# Revit family: Hager-UNIVERS-Surface_mounted-IP44-With_Cover-With_DIN-NoHosted-PT-pt
name_source: partatom
category: Electrical Equipment
units: mm (PartAtom-declared; Revit-internal decimal feet)

## family parameters
Always vertical = Yes
Cut with Voids When Loaded = No
Maintain Annotation Orientation = No
Panel Configuration = Two Columns, Circuits Across
Part Type = Panelboard
Room Calculation Point = No
Round Connector Dimension = Use Diameter
Shared = No
Work Plane-Based = Yes

## types (43) — shared parameters
Code hager = ADD-EC000214_EU
Default Elevation = 1200 mm
EF000007 - Colour = White
EF000024 - UV resistant = No
EF000049 - Depth = 165 mm
EF000116 - RAL-number = 9010
EF000118 - With mounting plate = No
EF000218 - Built-in depth = 161 mm  [stored 0.528215 ft]
EF001062 - EMC-version = No
EF001088 - Extension possible = Yes
EF001134 - DIN-rail = Yes
EF004462 - Type of closure = Other
EF005474 - Degree of protection (IP) = IP44
EF006306 - With lock = No
EF015941 - Signal passing door = No
ETIM class code = EC000214
ETIM class name = Small distribution board
HG000002-With door or cover = Yes
HG000003-Range = UNIVERS
HG000005-Thickness = 2 mm  [stored 0.00656168 ft]
HG000006-Flush mounted = No
HG000011-Empty rows from bottom = No
HG000012-Door swing angle = 90.00°
HG000013-Door on the left = No
HG000014-Door on the right = Yes
HG000015-Clearance visibility = Yes
HG000016-Door 3D visibility = Yes
HG000017-Distance between poles = 18 mm  [stored 0.0590551 ft]
HG000060-RAL-number = 9010
HG000099-Onfly Template ID = 507532
Manufacturer = Hager
Name BIM&CO = Electricity
Name hager = ADD_Enclosures_EC000214
Reference = Template-Enclosure_EU-EC000214
Uniformat = Low Tension Service & Dist.
Uniformat code = D501001
zero-valued in all types: EF001131 - Inner depth, HG000007-Number of empty columns

## per-type parameters (varying)
| type | BC_METADATA | EF000003 - Mounting method | EF000008 - Width | EF000040 - Height | EF000266 - Number of rows | EF000332 - Built-in height | EF000846 - Built-in width | EF002950 - Width in number of modular spacings | EF006244 - Transparent cover/door | EF009212 - Cover model | EF015776 - Earthing terminal block | EF015777 - Neutral terminal block | HG000001-Number of columns | HG000004-Manufacturer reference | HG000008-Number of empty rows | HG000009-Double swing door | HG000010-Asymmetric doors | HGEF000266-Number of rows | HGEF002950-Width in number of modular spacings |
| UNIVERS-Surface_mounted_W800_H800_D165_36_Modular_Spacing-FWB53N | {"ObjectGuid":"e7c7e345-cd60-4a16-9c19-dfa0064b8dbf","ModelGuid":"5f3c90c3-36aa-4b6e-8de8-4e54ba171ab8","VariantGuid":"0449715e-91fc-4989-86f3-c886387d58d4","Revision":"#3","VariantName":"UNIVERS-Surface_mounted_W800_H800_D165_36_Modular_Spacing-FWB53N"} | Surface mounted | 800 mm  [stored 2.62467 ft] | 800 mm  [stored 2.62467 ft] | 5 | 800 mm  [stored 2.62467 ft] | 800 mm  [stored 2.62467 ft] | 36 | No | With notch | No | No | 3 | FWB53N | 2 | Yes | Yes | 5 | 36 |
| UNIVERS-Surface_mounted_W800_H800_D165_36_Modular_Spacing-FWB53S | {"ObjectGuid":"e7c7e345-cd60-4a16-9c19-dfa0064b8dbf","ModelGuid":"5f3c90c3-36aa-4b6e-8de8-4e54ba171ab8","VariantGuid":"70780475-1a53-44c7-8c09-04e4199d2f75","Revision":"#3","VariantName":"UNIVERS-Surface_mounted_W800_H800_D165_36_Modular_Spacing-FWB53S"} | Surface mounted | 800 mm  [stored 2.62467 ft] | 800 mm  [stored 2.62467 ft] | 5 | 800 mm  [stored 2.62467 ft] | 800 mm  [stored 2.62467 ft] | 36 | No | With notch | Yes | Yes | 3 | FWB53S | 0 | Yes | Yes | 5 | 36 |
| UNIVERS-Surface_mounted_W1050_H800_D165_48_Modular_Spacing-FWB54GS | {"ObjectGuid":"e7c7e345-cd60-4a16-9c19-dfa0064b8dbf","ModelGuid":"5f3c90c3-36aa-4b6e-8de8-4e54ba171ab8","VariantGuid":"5e6222b7-83c6-47e9-85ec-fb5e80a4b5de","Revision":"#3","VariantName":"UNIVERS-Surface_mounted_W1050_H800_D165_48_Modular_Spacing-FWB54GS"} | Surface mounted | 1050 mm  [stored 3.44488 ft] | 800 mm  [stored 2.62467 ft] | 5 | 800 mm  [stored 2.62467 ft] | 1050 mm  [stored 3.44488 ft] | 48 | Yes | With notch | Yes | Yes | 4 | FWB54GS | 0 | Yes | No | 5 | 48 |
| UNIVERS-Surface_mounted_W1050_H800_D165_48_Modular_Spacing-FWB54S | {"ObjectGuid":"e7c7e345-cd60-4a16-9c19-dfa0064b8dbf","ModelGuid":"5f3c90c3-36aa-4b6e-8de8-4e54ba171ab8","VariantGuid":"4e09de71-0c15-486c-be22-81b695f3b53c","Revision":"#3","VariantName":"UNIVERS-Surface_mounted_W1050_H800_D165_48_Modular_Spacing-FWB54S"} | Surface mounted | 1050 mm  [stored 3.44488 ft] | 800 mm  [stored 2.62467 ft] | 5 | 800 mm  [stored 2.62467 ft] | 1050 mm  [stored 3.44488 ft] | 48 | No | With notch | Yes | Yes | 4 | FWB54S | 0 | Yes | No | 5 | 48 |
| UNIVERS-Surface_mounted_W300_H950_D165_12_Modular_Spacing-FWB61S | {"ObjectGuid":"e7c7e345-cd60-4a16-9c19-dfa0064b8dbf","ModelGuid":"5f3c90c3-36aa-4b6e-8de8-4e54ba171ab8","VariantGuid":"d75a9c82-e212-4b1c-91cf-2a02521cf286","Revision":"#3","VariantName":"UNIVERS-Surface_mounted_W300_H950_D165_12_Modular_Spacing-FWB61S"} | Surface mounted | 300 mm | 950 mm  [stored 3.1168 ft] | 6 | 950 mm  [stored 3.1168 ft] | 300 mm | 12 | No | With notch | Yes | Yes | 1 | FWB61S | 0 | No | No | 6 | 12 |
| UNIVERS-Surface_mounted_W550_H950_D165_24_Modular_Spacing-FWB62GS | {"ObjectGuid":"e7c7e345-cd60-4a16-9c19-dfa0064b8dbf","ModelGuid":"5f3c90c3-36aa-4b6e-8de8-4e54ba171ab8","VariantGuid":"d2d455f6-8088-4d0c-b9d0-a91f4a603c26","Revision":"#3","VariantName":"UNIVERS-Surface_mounted_W550_H950_D165_24_Modular_Spacing-FWB62GS"} | Surface mounted | 550 mm | 950 mm  [stored 3.1168 ft] | 6 | 950 mm  [stored 3.1168 ft] | 550 mm | 24 | Yes | With notch | Yes | Yes | 2 | FWB62GS | 0 | No | No | 6 | 24 |
| UNIVERS-Surface_mounted_W550_H950_D165_26_Modular_Spacing-FWB62M2 | {"ObjectGuid":"e7c7e345-cd60-4a16-9c19-dfa0064b8dbf","ModelGuid":"5f3c90c3-36aa-4b6e-8de8-4e54ba171ab8","VariantGuid":"2e5a0d4c-b45d-4552-9a05-bd38f025c8f6","Revision":"#3","VariantName":"UNIVERS-Surface_mounted_W550_H950_D165_26_Modular_Spacing-FWB62M2"} | Surface mounted | 550 mm | 950 mm  [stored 3.1168 ft] | 6 | 950 mm  [stored 3.1168 ft] | 550 mm | 26 | No | Closed | No | No | 1 | FWB62M2 | 0 | No | No | 6 | 26 |
| UNIVERS-Surface_mounted_W550_H950_D165_24_Modular_Spacing-FWB62N | {"ObjectGuid":"e7c7e345-cd60-4a16-9c19-dfa0064b8dbf","ModelGuid":"5f3c90c3-36aa-4b6e-8de8-4e54ba171ab8","VariantGuid":"0534ccd4-eb5c-456c-84bc-d0c8a7f9486a","Revision":"#3","VariantName":"UNIVERS-Surface_mounted_W550_H950_D165_24_Modular_Spacing-FWB62N"} | Surface mounted | 550 mm | 950 mm  [stored 3.1168 ft] | 6 | 950 mm  [stored 3.1168 ft] | 550 mm | 24 | No | With notch | No | No | 2 | FWB62N | 2 | No | No | 6 | 24 |
| UNIVERS-Surface_mounted_W300_H500_D165_12_Modular_Spacing-FWB31S | {"ObjectGuid":"e7c7e345-cd60-4a16-9c19-dfa0064b8dbf","ModelGuid":"5f3c90c3-36aa-4b6e-8de8-4e54ba171ab8","VariantGuid":"9bf5f36f-aab7-4db9-9452-cf65efd598aa","Revision":"#3","VariantName":"UNIVERS-Surface_mounted_W300_H500_D165_12_Modular_Spacing-FWB31S"} | Surface mounted | 300 mm | 500 mm  [stored 1.64042 ft] | 3 | 500 mm  [stored 1.64042 ft] | 300 mm | 12 | No | With notch | Yes | Yes | 1 | FWB31S | 0 | No | No | 3 | 12 |
| UNIVERS-Surface_mounted_W550_H500_D165_24_Modular_Spacing-FWB32GS | {"ObjectGuid":"e7c7e345-cd60-4a16-9c19-dfa0064b8dbf","ModelGuid":"5f3c90c3-36aa-4b6e-8de8-4e54ba171ab8","VariantGuid":"fb7a85dd-3230-4837-b0c0-b72064a3e6fe","Revision":"#3","VariantName":"UNIVERS-Surface_mounted_W550_H500_D165_24_Modular_Spacing-FWB32GS"} | Surface mounted | 550 mm | 500 mm  [stored 1.64042 ft] | 3 | 500 mm  [stored 1.64042 ft] | 550 mm | 24 | Yes | With notch | Yes | Yes | 2 | FWB32GS | 0 | No | No | 3 | 24 |
| UNIVERS-Surface_mounted_W550_H500_D165_26_Modular_Spacing-FWB32M2 | {"ObjectGuid":"e7c7e345-cd60-4a16-9c19-dfa0064b8dbf","ModelGuid":"5f3c90c3-36aa-4b6e-8de8-4e54ba171ab8","VariantGuid":"f52a0b61-ad72-444d-9360-4d9b0c4974fd","Revision":"#3","VariantName":"UNIVERS-Surface_mounted_W550_H500_D165_26_Modular_Spacing-FWB32M2"} | Surface mounted | 550 mm | 500 mm  [stored 1.64042 ft] | 3 | 500 mm  [stored 1.64042 ft] | 550 mm | 26 | No | Closed | No | No | 1 | FWB32M2 | 0 | No | No | 3 | 26 |
| UNIVERS-Surface_mounted_W550_H500_D165_24_Modular_Spacing-FWB32S | {"ObjectGuid":"e7c7e345-cd60-4a16-9c19-dfa0064b8dbf","ModelGuid":"5f3c90c3-36aa-4b6e-8de8-4e54ba171ab8","VariantGuid":"5a80b1ac-59b3-4e31-a08f-5cec29b1deb8","Revision":"#3","VariantName":"UNIVERS-Surface_mounted_W550_H500_D165_24_Modular_Spacing-FWB32S"} | Surface mounted | 550 mm | 500 mm  [stored 1.64042 ft] | 3 | 500 mm  [stored 1.64042 ft] | 550 mm | 24 | No | With notch | Yes | Yes | 2 | FWB32S | 0 | No | No | 3 | 24 |
| UNIVERS-Surface_mounted_W800_H500_D165_36_Modular_Spacing-FWB33S | {"ObjectGuid":"e7c7e345-cd60-4a16-9c19-dfa0064b8dbf","ModelGuid":"5f3c90c3-36aa-4b6e-8de8-4e54ba171ab8","VariantGuid":"35a470b6-89d0-4b4f-96af-1046d63bd483","Revision":"#3","VariantName":"UNIVERS-Surface_mounted_W800_H500_D165_36_Modular_Spacing-FWB33S"} | Surface mounted | 800 mm  [stored 2.62467 ft] | 500 mm  [stored 1.64042 ft] | 3 | 500 mm  [stored 1.64042 ft] | 800 mm  [stored 2.62467 ft] | 36 | No | With notch | Yes | Yes | 3 | FWB33S | 0 | Yes | Yes | 3 | 36 |
| UNIVERS-Surface_mounted_W1050_H500_D165_48_Modular_Spacing-FWB34GS | {"ObjectGuid":"e7c7e345-cd60-4a16-9c19-dfa0064b8dbf","ModelGuid":"5f3c90c3-36aa-4b6e-8de8-4e54ba171ab8","VariantGuid":"be8cd02b-23f5-4942-b7b3-b5a2112c5854","Revision":"#3","VariantName":"UNIVERS-Surface_mounted_W1050_H500_D165_48_Modular_Spacing-FWB34GS"} | Surface mounted | 1050 mm  [stored 3.44488 ft] | 500 mm  [stored 1.64042 ft] | 3 | 500 mm  [stored 1.64042 ft] | 1050 mm  [stored 3.44488 ft] | 48 | Yes | With notch | Yes | Yes | 4 | FWB34GS | 0 | Yes | No | 3 | 48 |
| UNIVERS-Surface_mounted_W1050_H500_D165_48_Modular_Spacing-FWB34S | {"ObjectGuid":"e7c7e345-cd60-4a16-9c19-dfa0064b8dbf","ModelGuid":"5f3c90c3-36aa-4b6e-8de8-4e54ba171ab8","VariantGuid":"cc12be3d-891f-44bf-81d6-319a16d03e2f","Revision":"#3","VariantName":"UNIVERS-Surface_mounted_W1050_H500_D165_48_Modular_Spacing-FWB34S"} | Surface mounted | 1050 mm  [stored 3.44488 ft] | 500 mm  [stored 1.64042 ft] | 3 | 500 mm  [stored 1.64042 ft] | 1050 mm  [stored 3.44488 ft] | 48 | No | With notch | Yes | Yes | 4 | FWB34S | 0 | Yes | No | 3 | 48 |
| UNIVERS-Surface_mounted_W300_H650_D165_12_Modular_Spacing-FWB41S | {"ObjectGuid":"e7c7e345-cd60-4a16-9c19-dfa0064b8dbf","ModelGuid":"5f3c90c3-36aa-4b6e-8de8-4e54ba171ab8","VariantGuid":"5ece5d32-3d52-4811-be08-8941b2c84f9b","Revision":"#3","VariantName":"UNIVERS-Surface_mounted_W300_H650_D165_12_Modular_Spacing-FWB41S"} | Surface mounted | 300 mm | 650 mm  [stored 2.13255 ft] | 4 | 650 mm  [stored 2.13255 ft] | 300 mm | 12 | No | With notch | Yes | Yes | 1 | FWB41S | 0 | No | No | 4 | 12 |
| UNIVERS-Surface_mounted_W550_H650_D165_24_Modular_Spacing-FWB42GS | {"ObjectGuid":"e7c7e345-cd60-4a16-9c19-dfa0064b8dbf","ModelGuid":"5f3c90c3-36aa-4b6e-8de8-4e54ba171ab8","VariantGuid":"4800a197-08de-4eea-944b-05a1431e3091","Revision":"#3","VariantName":"UNIVERS-Surface_mounted_W550_H650_D165_24_Modular_Spacing-FWB42GS"} | Surface mounted | 550 mm | 650 mm  [stored 2.13255 ft] | 4 | 650 mm  [stored 2.13255 ft] | 550 mm | 24 | Yes | With notch | Yes | Yes | 2 | FWB42GS | 0 | No | No | 4 | 24 |
| UNIVERS-Surface_mounted_W550_H650_D165_26_Modular_Spacing-FWB42M2 | {"ObjectGuid":"e7c7e345-cd60-4a16-9c19-dfa0064b8dbf","ModelGuid":"5f3c90c3-36aa-4b6e-8de8-4e54ba171ab8","VariantGuid":"ff45878f-ee16-4e91-9788-272bdf2cb385","Revision":"#3","VariantName":"UNIVERS-Surface_mounted_W550_H650_D165_26_Modular_Spacing-FWB42M2"} | Surface mounted | 550 mm | 650 mm  [stored 2.13255 ft] | 4 | 650 mm  [stored 2.13255 ft] | 550 mm | 26 | No | Closed | No | No | 1 | FWB42M2 | 0 | No | No | 4 | 26 |
| UNIVERS-Surface_mounted_W550_H650_D165_24_Modular_Spacing-FWB42S | {"ObjectGuid":"e7c7e345-cd60-4a16-9c19-dfa0064b8dbf","ModelGuid":"5f3c90c3-36aa-4b6e-8de8-4e54ba171ab8","VariantGuid":"a7ff8edd-fea0-4138-8384-63f245e46ff6","Revision":"#3","VariantName":"UNIVERS-Surface_mounted_W550_H650_D165_24_Modular_Spacing-FWB42S"} | Surface mounted/recessed mounted | 550 mm | 650 mm  [stored 2.13255 ft] | 4 | 650 mm  [stored 2.13255 ft] | 550 mm | 24 | No | With notch | Yes | Yes | 2 | FWB42S | 0 | No | No | 4 | 24 |
| UNIVERS-Surface_mounted_W800_H650_D165_36_Modular_Spacing-FWB43S | {"ObjectGuid":"e7c7e345-cd60-4a16-9c19-dfa0064b8dbf","ModelGuid":"5f3c90c3-36aa-4b6e-8de8-4e54ba171ab8","VariantGuid":"694371a0-3cfb-4381-bc54-f25bbc3fdddb","Revision":"#3","VariantName":"UNIVERS-Surface_mounted_W800_H650_D165_36_Modular_Spacing-FWB43S"} | Surface mounted | 800 mm  [stored 2.62467 ft] | 650 mm  [stored 2.13255 ft] | 4 | 650 mm  [stored 2.13255 ft] | 800 mm  [stored 2.62467 ft] | 36 | No | With notch | Yes | Yes | 3 | FWB43S | 0 | Yes | Yes | 4 | 36 |
| UNIVERS-Surface_mounted_W1050_H650_D165_48_Modular_Spacing-FWB44GS | {"ObjectGuid":"e7c7e345-cd60-4a16-9c19-dfa0064b8dbf","ModelGuid":"5f3c90c3-36aa-4b6e-8de8-4e54ba171ab8","VariantGuid":"80b9d9d5-fd64-4f73-886d-269bf54e62dc","Revision":"#3","VariantName":"UNIVERS-Surface_mounted_W1050_H650_D165_48_Modular_Spacing-FWB44GS"} | Surface mounted | 1050 mm  [stored 3.44488 ft] | 650 mm  [stored 2.13255 ft] | 4 | 650 mm  [stored 2.13255 ft] | 1050 mm  [stored 3.44488 ft] | 48 | Yes | With notch | Yes | Yes | 4 | FWB44GS | 0 | Yes | No | 4 | 48 |
| UNIVERS-Surface_mounted_W1050_H650_D165_48_Modular_Spacing-FWB44S | {"ObjectGuid":"e7c7e345-cd60-4a16-9c19-dfa0064b8dbf","ModelGuid":"5f3c90c3-36aa-4b6e-8de8-4e54ba171ab8","VariantGuid":"958c4d4e-67ea-4ca2-b1af-8047328ca48a","Revision":"#3","VariantName":"UNIVERS-Surface_mounted_W1050_H650_D165_48_Modular_Spacing-FWB44S"} | Surface mounted | 1050 mm  [stored 3.44488 ft] | 650 mm  [stored 2.13255 ft] | 4 | 650 mm  [stored 2.13255 ft] | 1050 mm  [stored 3.44488 ft] | 48 | No | With notch | Yes | Yes | 4 | FWB44S | 0 | Yes | No | 4 | 48 |
| UNIVERS-Surface_mounted_W300_H800_D165_12_Modular_Spacing-FWB51S | {"ObjectGuid":"e7c7e345-cd60-4a16-9c19-dfa0064b8dbf","ModelGuid":"5f3c90c3-36aa-4b6e-8de8-4e54ba171ab8","VariantGuid":"485017d3-d1a1-4c50-9960-5198ff632122","Revision":"#3","VariantName":"UNIVERS-Surface_mounted_W300_H800_D165_12_Modular_Spacing-FWB51S"} | Surface mounted | 300 mm | 800 mm  [stored 2.62467 ft] | 5 | 800 mm  [stored 2.62467 ft] | 300 mm | 12 | No | With notch | Yes | Yes | 1 | FWB51S | 0 | No | No | 5 | 12 |
| UNIVERS-Surface_mounted_W550_H800_D165_24_Modular_Spacing-FWB52GS | {"ObjectGuid":"e7c7e345-cd60-4a16-9c19-dfa0064b8dbf","ModelGuid":"5f3c90c3-36aa-4b6e-8de8-4e54ba171ab8","VariantGuid":"8440c55c-928c-4a66-a384-c63e5e9be550","Revision":"#3","VariantName":"UNIVERS-Surface_mounted_W550_H800_D165_24_Modular_Spacing-FWB52GS"} | Surface mounted | 550 mm | 800 mm  [stored 2.62467 ft] | 5 | 800 mm  [stored 2.62467 ft] | 550 mm | 24 | Yes | With notch | Yes | Yes | 2 | FWB52GS | 0 | No | No | 5 | 24 |
| UNIVERS-Surface_mounted_W550_H800_D165_26_Modular_Spacing-FWB52M2 | {"ObjectGuid":"e7c7e345-cd60-4a16-9c19-dfa0064b8dbf","ModelGuid":"5f3c90c3-36aa-4b6e-8de8-4e54ba171ab8","VariantGuid":"84c6e0b0-84ba-43f9-8486-ac857d178bdd","Revision":"#3","VariantName":"UNIVERS-Surface_mounted_W550_H800_D165_26_Modular_Spacing-FWB52M2"} | Surface mounted | 550 mm | 800 mm  [stored 2.62467 ft] | 5 | 800 mm  [stored 2.62467 ft] | 550 mm | 26 | No | Closed | No | No | 1 | FWB52M2 | 0 | No | No | 5 | 26 |
| UNIVERS-Surface_mounted_W550_H800_D165_24_Modular_Spacing-FWB52N | {"ObjectGuid":"e7c7e345-cd60-4a16-9c19-dfa0064b8dbf","ModelGuid":"5f3c90c3-36aa-4b6e-8de8-4e54ba171ab8","VariantGuid":"eb04def6-35ae-4f01-a42c-74ccab6b1dd4","Revision":"#3","VariantName":"UNIVERS-Surface_mounted_W550_H800_D165_24_Modular_Spacing-FWB52N"} | Surface mounted | 550 mm | 800 mm  [stored 2.62467 ft] | 5 | 800 mm  [stored 2.62467 ft] | 550 mm | 24 | No | With notch | No | No | 2 | FWB52N | 2 | No | No | 5 | 24 |
| UNIVERS-Surface_mounted_W550_H800_D165_24_Modular_Spacing-FWB52S | {"ObjectGuid":"e7c7e345-cd60-4a16-9c19-dfa0064b8dbf","ModelGuid":"5f3c90c3-36aa-4b6e-8de8-4e54ba171ab8","VariantGuid":"11957740-69cf-4a1b-bfa0-25a853491458","Revision":"#3","VariantName":"UNIVERS-Surface_mounted_W550_H800_D165_24_Modular_Spacing-FWB52S"} | Surface mounted | 550 mm | 800 mm  [stored 2.62467 ft] | 5 | 800 mm  [stored 2.62467 ft] | 550 mm | 24 | No | With notch | Yes | Yes | 2 | FWB52S | 0 | No | No | 5 | 24 |
| UNIVERS-Surface_mounted_W550_H950_D165_24_Modular_Spacing-FWB62S | {"ObjectGuid":"e7c7e345-cd60-4a16-9c19-dfa0064b8dbf","ModelGuid":"5f3c90c3-36aa-4b6e-8de8-4e54ba171ab8","VariantGuid":"77259382-65aa-4b1e-869a-cfa50e7e1151","Revision":"#3","VariantName":"UNIVERS-Surface_mounted_W550_H950_D165_24_Modular_Spacing-FWB62S"} | Surface mounted | 550 mm | 950 mm  [stored 3.1168 ft] | 6 | 950 mm  [stored 3.1168 ft] | 550 mm | 24 | No | With notch | Yes | Yes | 2 | FWB62S | 0 | No | No | 6 | 24 |
| UNIVERS-Surface_mounted_W800_H950_D165_36_Modular_Spacing-FWB63N | {"ObjectGuid":"e7c7e345-cd60-4a16-9c19-dfa0064b8dbf","ModelGuid":"5f3c90c3-36aa-4b6e-8de8-4e54ba171ab8","VariantGuid":"cb41e5b3-02c2-4750-a6e5-7048ffe01e97","Revision":"#3","VariantName":"UNIVERS-Surface_mounted_W800_H950_D165_36_Modular_Spacing-FWB63N"} | Surface mounted | 800 mm  [stored 2.62467 ft] | 950 mm  [stored 3.1168 ft] | 6 | 950 mm  [stored 3.1168 ft] | 800 mm  [stored 2.62467 ft] | 36 | No | With notch | No | No | 3 | FWB63N | 2 | Yes | Yes | 6 | 36 |
| UNIVERS-Surface_mounted_W800_H950_D165_36_Modular_Spacing-FWB63S | {"ObjectGuid":"e7c7e345-cd60-4a16-9c19-dfa0064b8dbf","ModelGuid":"5f3c90c3-36aa-4b6e-8de8-4e54ba171ab8","VariantGuid":"f41a47f8-f480-46dd-a0ef-3e98abfe04c0","Revision":"#3","VariantName":"UNIVERS-Surface_mounted_W800_H950_D165_36_Modular_Spacing-FWB63S"} | Surface mounted | 800 mm  [stored 2.62467 ft] | 950 mm  [stored 3.1168 ft] | 6 | 950 mm  [stored 3.1168 ft] | 800 mm  [stored 2.62467 ft] | 36 | No | With notch | Yes | Yes | 3 | FWB63S | 0 | Yes | Yes | 6 | 36 |
| UNIVERS-Surface_mounted_W1050_H950_D165_48_Modular_Spacing-FWB64GS | {"ObjectGuid":"e7c7e345-cd60-4a16-9c19-dfa0064b8dbf","ModelGuid":"5f3c90c3-36aa-4b6e-8de8-4e54ba171ab8","VariantGuid":"3c734a3f-374f-4c5e-822b-aceaff54270b","Revision":"#3","VariantName":"UNIVERS-Surface_mounted_W1050_H950_D165_48_Modular_Spacing-FWB64GS"} | Surface mounted | 1050 mm  [stored 3.44488 ft] | 950 mm  [stored 3.1168 ft] | 6 | 950 mm  [stored 3.1168 ft] | 1050 mm  [stored 3.44488 ft] | 48 | Yes | With notch | Yes | Yes | 4 | FWB64GS | 0 | Yes | No | 6 | 48 |
| UNIVERS-Surface_mounted_W1050_H950_D165_48_Modular_Spacing-FWB64N | {"ObjectGuid":"e7c7e345-cd60-4a16-9c19-dfa0064b8dbf","ModelGuid":"5f3c90c3-36aa-4b6e-8de8-4e54ba171ab8","VariantGuid":"99b5a869-c00c-4308-92dd-7e31dc713ef3","Revision":"#3","VariantName":"UNIVERS-Surface_mounted_W1050_H950_D165_48_Modular_Spacing-FWB64N"} | Surface mounted | 1050 mm  [stored 3.44488 ft] | 950 mm  [stored 3.1168 ft] | 6 | 950 mm  [stored 3.1168 ft] | 1050 mm  [stored 3.44488 ft] | 48 | No | With notch | No | No | 4 | FWB64N | 2 | Yes | No | 6 | 48 |
| UNIVERS-Surface_mounted_W1050_H950_D165_48_Modular_Spacing-FWB64S | {"ObjectGuid":"e7c7e345-cd60-4a16-9c19-dfa0064b8dbf","ModelGuid":"5f3c90c3-36aa-4b6e-8de8-4e54ba171ab8","VariantGuid":"fc1a7d38-a105-4c3a-b171-c45a80d5c211","Revision":"#3","VariantName":"UNIVERS-Surface_mounted_W1050_H950_D165_48_Modular_Spacing-FWB64S"} | Surface mounted | 1050 mm  [stored 3.44488 ft] | 950 mm  [stored 3.1168 ft] | 6 | 950 mm  [stored 3.1168 ft] | 1050 mm  [stored 3.44488 ft] | 48 | No | With notch | Yes | Yes | 4 | FWB64S | 0 | Yes | No | 6 | 48 |
| UNIVERS-Surface_mounted_W300_H1100_D165_12_Modular_Spacing-FWB71S | {"ObjectGuid":"e7c7e345-cd60-4a16-9c19-dfa0064b8dbf","ModelGuid":"5f3c90c3-36aa-4b6e-8de8-4e54ba171ab8","VariantGuid":"1162c4e2-4707-4c66-80c0-3641417c3d5d","Revision":"#3","VariantName":"UNIVERS-Surface_mounted_W300_H1100_D165_12_Modular_Spacing-FWB71S"} | Surface mounted | 300 mm | 1100 mm | 7 | 1100 mm | 300 mm | 12 | No | With notch | Yes | Yes | 1 | FWB71S | 0 | No | No | 7 | 12 |
| UNIVERS-Surface_mounted_W550_H1100_D165_24_Modular_Spacing-FWB72GS | {"ObjectGuid":"e7c7e345-cd60-4a16-9c19-dfa0064b8dbf","ModelGuid":"5f3c90c3-36aa-4b6e-8de8-4e54ba171ab8","VariantGuid":"1073677e-2332-4886-b88c-450902d7afb2","Revision":"#3","VariantName":"UNIVERS-Surface_mounted_W550_H1100_D165_24_Modular_Spacing-FWB72GS"} | Surface mounted | 550 mm | 1100 mm | 7 | 1100 mm | 550 mm | 24 | Yes | With notch | Yes | Yes | 2 | FWB72GS | 0 | No | No | 7 | 24 |
| UNIVERS-Surface_mounted_W550_H1100_D165_26_Modular_Spacing-FWB72M2 | {"ObjectGuid":"e7c7e345-cd60-4a16-9c19-dfa0064b8dbf","ModelGuid":"5f3c90c3-36aa-4b6e-8de8-4e54ba171ab8","VariantGuid":"e9ae9ba9-4b2d-457f-8518-17f23ba72496","Revision":"#3","VariantName":"UNIVERS-Surface_mounted_W550_H1100_D165_26_Modular_Spacing-FWB72M2"} | Surface mounted | 550 mm | 1100 mm | 7 | 1100 mm | 550 mm | 26 | No | Closed | No | No | 1 | FWB72M2 | 0 | No | No | 7 | 26 |
| UNIVERS-Surface_mounted_W550_H1100_D165_24_Modular_Spacing-FWB72N | {"ObjectGuid":"e7c7e345-cd60-4a16-9c19-dfa0064b8dbf","ModelGuid":"5f3c90c3-36aa-4b6e-8de8-4e54ba171ab8","VariantGuid":"9b3d0d46-4185-4263-a863-ceeb59a03e55","Revision":"#3","VariantName":"UNIVERS-Surface_mounted_W550_H1100_D165_24_Modular_Spacing-FWB72N"} | Surface mounted | 550 mm | 1100 mm | 7 | 1100 mm | 550 mm | 24 | No | With notch | No | No | 2 | FWB72N | 2 | No | No | 7 | 24 |
| UNIVERS-Surface_mounted_W550_H1100_D165_24_Modular_Spacing-FWB72S | {"ObjectGuid":"e7c7e345-cd60-4a16-9c19-dfa0064b8dbf","ModelGuid":"5f3c90c3-36aa-4b6e-8de8-4e54ba171ab8","VariantGuid":"445bf463-9c32-4663-a28f-c9ee8c4d4b0a","Revision":"#3","VariantName":"UNIVERS-Surface_mounted_W550_H1100_D165_24_Modular_Spacing-FWB72S"} | Surface mounted/recessed mounted | 550 mm | 1100 mm | 7 | 1100 mm | 550 mm | 24 | No | With notch | Yes | Yes | 2 | FWB72S | 0 | No | No | 7 | 24 |
| UNIVERS-Surface_mounted_W800_H1100_D165_36_Modular_Spacing-FWB73N | {"ObjectGuid":"e7c7e345-cd60-4a16-9c19-dfa0064b8dbf","ModelGuid":"5f3c90c3-36aa-4b6e-8de8-4e54ba171ab8","VariantGuid":"04a48d7d-38a8-4c0c-8176-d726367cf028","Revision":"#3","VariantName":"UNIVERS-Surface_mounted_W800_H1100_D165_36_Modular_Spacing-FWB73N"} | Surface mounted | 800 mm  [stored 2.62467 ft] | 1100 mm | 7 | 1100 mm | 800 mm  [stored 2.62467 ft] | 36 | No | With notch | No | No | 3 | FWB73N | 2 | Yes | Yes | 7 | 36 |
| UNIVERS-Surface_mounted_W800_H1100_D165_36_Modular_Spacing-FWB73S | {"ObjectGuid":"e7c7e345-cd60-4a16-9c19-dfa0064b8dbf","ModelGuid":"5f3c90c3-36aa-4b6e-8de8-4e54ba171ab8","VariantGuid":"ed86485a-baed-4e1b-a788-ea24cafcc3ad","Revision":"#3","VariantName":"UNIVERS-Surface_mounted_W800_H1100_D165_36_Modular_Spacing-FWB73S"} | Surface mounted/recessed mounted | 800 mm  [stored 2.62467 ft] | 1100 mm | 7 | 1100 mm | 800 mm  [stored 2.62467 ft] | 36 | No | With notch | Yes | Yes | 3 | FWB73S | 0 | Yes | Yes | 7 | 36 |
| UNIVERS-Surface_mounted_W1050_H1100_D165_48_Modular_Spacing-FWB74GS | {"ObjectGuid":"e7c7e345-cd60-4a16-9c19-dfa0064b8dbf","ModelGuid":"5f3c90c3-36aa-4b6e-8de8-4e54ba171ab8","VariantGuid":"6318ced9-a5ee-48cd-ae59-74e0c4b8c5a5","Revision":"#3","VariantName":"UNIVERS-Surface_mounted_W1050_H1100_D165_48_Modular_Spacing-FWB74GS"} | Surface mounted | 1050 mm  [stored 3.44488 ft] | 1100 mm | 7 | 1100 mm | 1050 mm  [stored 3.44488 ft] | 48 | Yes | With notch | Yes | Yes | 4 | FWB74GS | 0 | Yes | No | 7 | 48 |
| UNIVERS-Surface_mounted_W1050_H1100_D165_48_Modular_Spacing-FWB74N | {"ObjectGuid":"e7c7e345-cd60-4a16-9c19-dfa0064b8dbf","ModelGuid":"5f3c90c3-36aa-4b6e-8de8-4e54ba171ab8","VariantGuid":"70ad40dd-57cd-4dc8-a8a4-1acb9c9df259","Revision":"#3","VariantName":"UNIVERS-Surface_mounted_W1050_H1100_D165_48_Modular_Spacing-FWB74N"} | Surface mounted | 1050 mm  [stored 3.44488 ft] | 1100 mm | 7 | 1100 mm | 1050 mm  [stored 3.44488 ft] | 48 | No | With notch | No | No | 4 | FWB74N | 2 | Yes | No | 7 | 48 |
| UNIVERS-Surface_mounted_W1050_H1100_D165_48_Modular_Spacing-FWB74S | {"ObjectGuid":"e7c7e345-cd60-4a16-9c19-dfa0064b8dbf","ModelGuid":"5f3c90c3-36aa-4b6e-8de8-4e54ba171ab8","VariantGuid":"ca6fa26e-fd80-4b98-aff9-17a56689c54d","Revision":"#3","VariantName":"UNIVERS-Surface_mounted_W1050_H1100_D165_48_Modular_Spacing-FWB74S"} | Surface mounted/recessed mounted | 1050 mm  [stored 3.44488 ft] | 1100 mm | 7 | 1100 mm | 1050 mm  [stored 3.44488 ft] | 48 | No | With notch | Yes | Yes | 4 | FWB74S | 0 | Yes | No | 7 | 48 |

note: [stored X ft] marks values corroborated as IEEE doubles in the binary element streams (Revit-internal decimal feet)

## geometry (parser evidence)
native form markers: Sweep x17
no freeform markers — native parametric forms only
